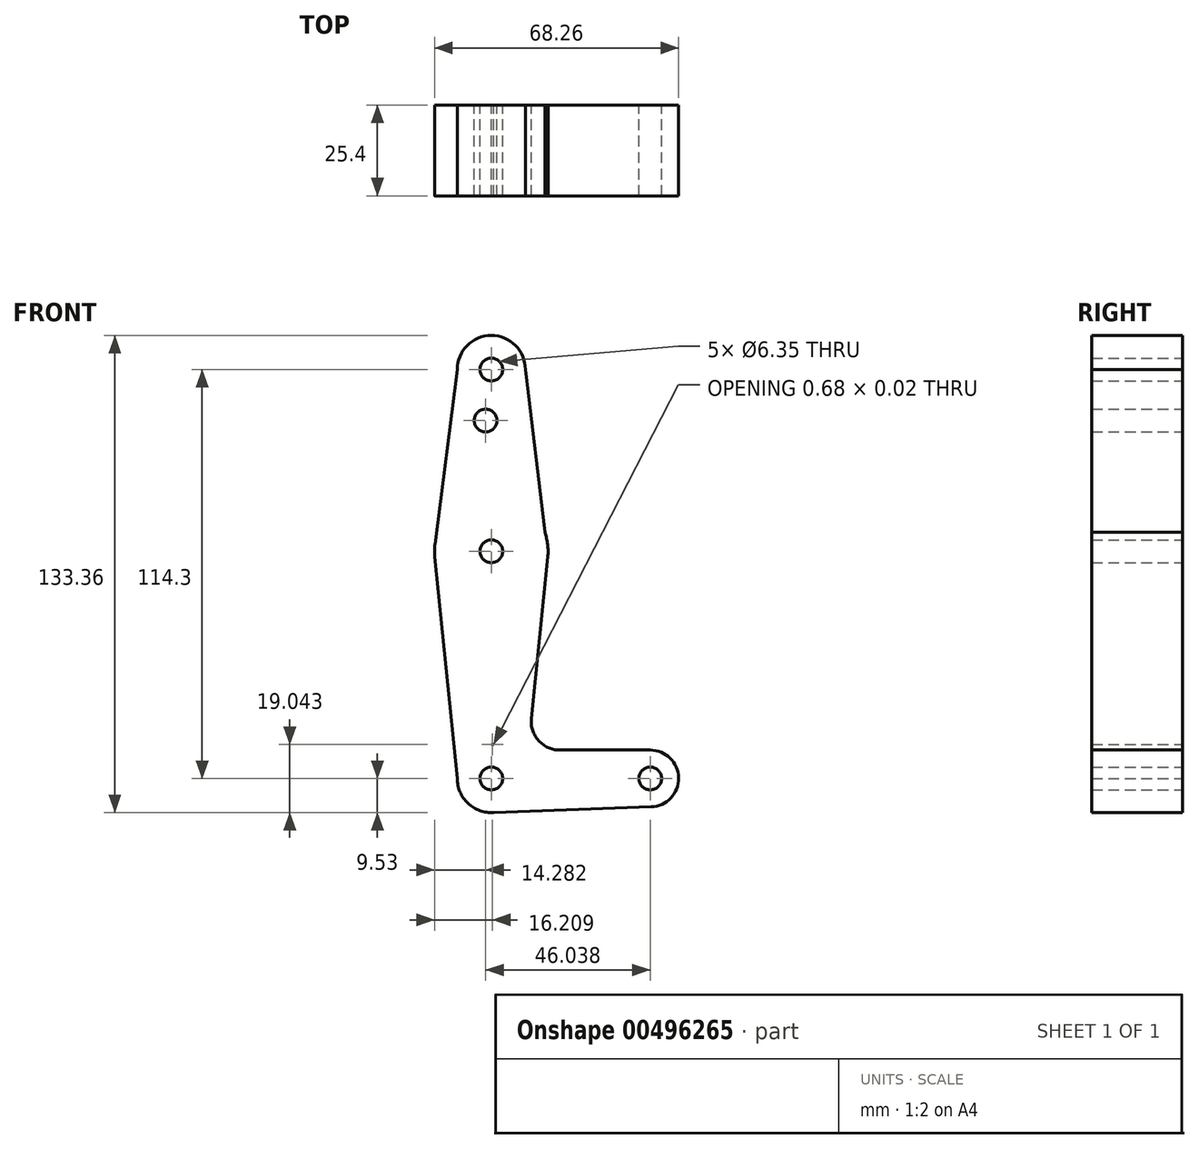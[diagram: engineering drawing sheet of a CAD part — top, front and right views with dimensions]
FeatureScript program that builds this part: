
annotation { "Feature Type Name" : "Feature", "Feature Type Description" : "" }
export const myFeature = defineFeature(function(context is Context, id is Id, definition is map)
    precondition{}
    {
        {
            var Q0;
            Q0=qCreatedBy(makeId("Front.planeOp"),FACE);
            var sketch = newSketch(context, id + "F0", { "sketchPlane" : qUnion([Q0])});
            skLineSegment(sketch, "E0", {"start": v(0, 0) * mm, "end": v(0, 114.3) * mm, "construction": true});
            skLineSegment(sketch, "E1", {"start": v(0, 0) * mm, "end": v(44.45, 0) * mm, "construction": true});
            skCircle(sketch, "E2", {"center": v(0, 114.3) * mm, "radius": 9.53 * mm});
            skCircle(sketch, "E3", {"center": v(0, 63.5) * mm, "radius": 15.88 * mm});
            skCircle(sketch, "E4", {"center": v(0, 0) * mm, "radius": 9.53 * mm});
            skCircle(sketch, "E5", {"center": v(44.45, 0) * mm, "radius": 7.94 * mm});
            skLineSegment(sketch, "E6", {"start": v(0, -9.53) * mm, "end": v(44.73, -7.93) * mm});
            skLineSegment(sketch, "E7", {"start": v(0, 9.53) * mm, "end": v(3.05, 9.42) * mm});
            skCircle(sketch, "E8", {"center": v(0, 114.3) * mm, "radius": 3.18 * mm});
            skCircle(sketch, "E9", {"center": v(-1.59, 100.03) * mm, "radius": 3.18 * mm});
            skLineSegment(sketch, "E10", {"start": v(44.45, 7.94) * mm, "end": v(19.12, 7.94) * mm});
            skLineSegment(sketch, "E11", {"start": v(-15.75, 65.5) * mm, "end": v(-9.53, 114.3) * mm});
            skLineSegment(sketch, "E12", {"start": v(-9.53, 0) * mm, "end": v(-15.8, 61.9) * mm});
            skLineSegment(sketch, "E13", {"start": v(9.53, 114.3) * mm, "end": v(15.8, 61.9) * mm});
            skLineSegment(sketch, "E14", {"start": v(15.8, 61.9) * mm, "end": v(11.22, 16.69) * mm});
            skCircle(sketch, "E15", {"center": v(0, 63.5) * mm, "radius": 3.18 * mm});
            skCircle(sketch, "E16", {"center": v(44.45, 0) * mm, "radius": 3.18 * mm});
            skCircle(sketch, "E17", {"center": v(0, 0) * mm, "radius": 3.18 * mm});
            skArc(sketch, "E18.filletArc", {"start": v(11.22, 16.69) * mm, "mid": v(13.23, 10.56) * mm, "end": v(19.12, 7.94) * mm});
            skSolve(sketch);
        }
        {
            var Q0;
            Q0 = qSketchRegion(id + "F0", true);
            extrude(context, id + "F1", {"entities" : qUnion([Q0]), "depth" : 25.4 * mm});
        }
    });
